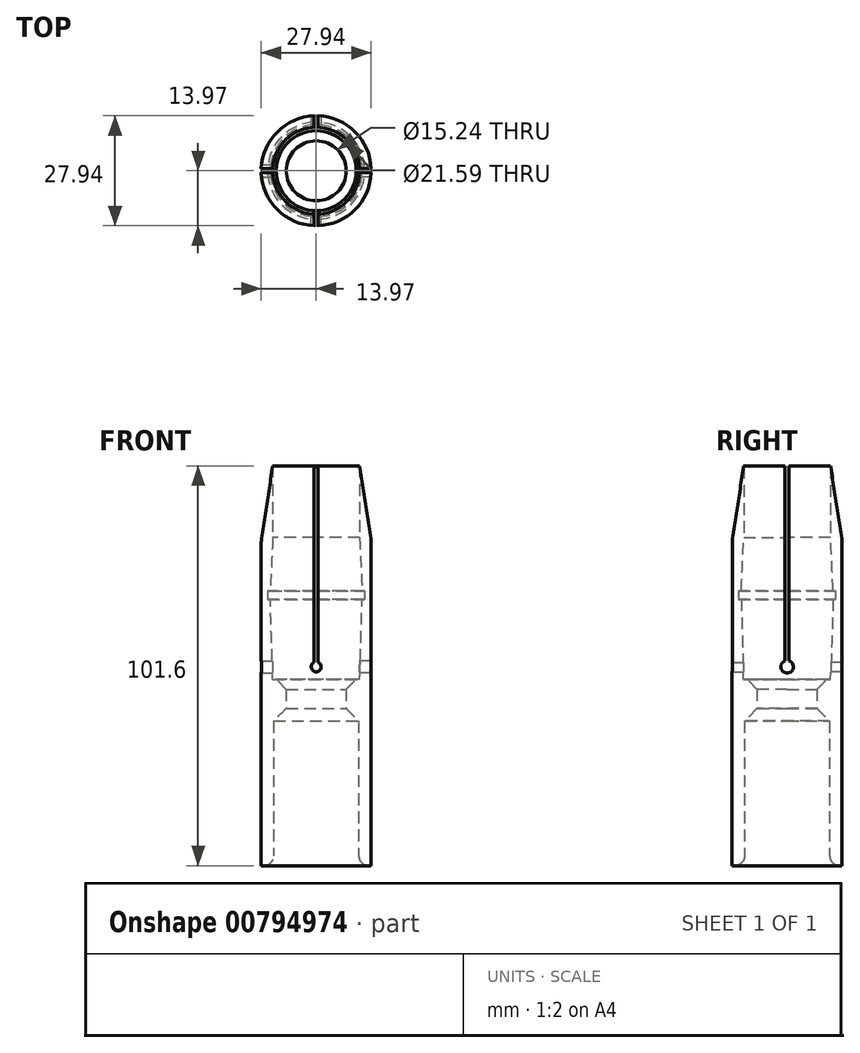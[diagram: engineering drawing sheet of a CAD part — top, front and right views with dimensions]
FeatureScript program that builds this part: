
annotation { "Feature Type Name" : "Feature", "Feature Type Description" : "" }
export const myFeature = defineFeature(function(context is Context, id is Id, definition is map)
    precondition{}
    {
        {
            var Q0;
            Q0=qCreatedBy(makeId("Front.planeOp"),FACE);
            var sketch = newSketch(context, id + "F0", { "sketchPlane" : qUnion([Q0])});
            skLineSegment(sketch, "E0.bottom", {"start": v(10.8, 0) * mm, "end": v(13.97, 0) * mm});
            skLineSegment(sketch, "E0.right", {"start": v(13.97, 0) * mm, "end": v(13.97, 82.55) * mm});
            skLineSegment(sketch, "E1", {"start": v(11.05, 101.6) * mm, "end": v(13.97, 82.55) * mm});
            skLineSegment(sketch, "E2", {"start": v(11.68, 69.85) * mm, "end": v(12.32, 69.85) * mm});
            skLineSegment(sketch, "E3", {"start": v(12.32, 69.85) * mm, "end": v(12.32, 67.7) * mm});
            skLineSegment(sketch, "E4", {"start": v(12.32, 67.7) * mm, "end": v(11.68, 67.7) * mm});
            skLineSegment(sketch, "E5", {"start": v(11.05, 47.37) * mm, "end": v(7.62, 47.37) * mm});
            skLineSegment(sketch, "E6", {"start": v(7.62, 47.37) * mm, "end": v(7.62, 39.95) * mm});
            skLineSegment(sketch, "E7.bottom", {"start": v(7.62, 39.95) * mm, "end": v(10.8, 39.95) * mm});
            skLineSegment(sketch, "E7.right", {"start": v(10.8, 39.95) * mm, "end": v(10.8, 0) * mm});
            skLineSegment(sketch, "E8", {"start": v(11.05, 101.6) * mm, "end": v(11.05, 83.35) * mm});
            skLineSegment(sketch, "E9", {"start": v(11.05, 83.35) * mm, "end": v(11.68, 69.85) * mm});
            skPoint(sketch, "E10", {"position": v(11.68, 67.7) * mm});
            skLineSegment(sketch, "E11", {"start": v(11.05, 47.37) * mm, "end": v(11.68, 67.7) * mm});
            skSolve(sketch);
        }
        {
            var Q0;
            Q0=qCreatedBy(makeId("Front.planeOp"),FACE);
            var sketch = newSketch(context, id + "F1", { "sketchPlane" : qUnion([Q0])});
            skLineSegment(sketch, "E12", {"start": v(0, -19.13) * mm, "end": v(0, 56.04) * mm});
            skSolve(sketch);
        }
        {
            var Q0;
            Q0=makeQuery(id+"F0.imprint","IMPRINT",FACE,{"disambiguationData":[TD([[makeQuery(id+"F0.imprint","IMPRINT",EDGE,{"derivedFrom":sQuery(id+"F0.wireOp",EDGE,"E0.bottom")}),1.0]])]});
            var Q1;
            Q1=sQuery(id+"F1.wireOp",EDGE,"E12");
            revolve(context, id + "F2", {"surfaceOperationType" : NewSurfaceOperationType.NEW, "entities" : qUnion([Q0]), "axis" : qUnion([Q1]), "revolveType" : RevolveType.FULL});
        }
        {
            var Q0;
            Q0=makeQuery(id+"F2.opRevolve","SWEPT_EDGE",EDGE,{"disambiguationData":[OSD([sQuery(id+"F0.wireOp",EDGE,"E0.bottom"),sQuery(id+"F0.wireOp",EDGE,"E7.right")])]});
            fillet(context, id + "F3", {"entities" : qUnion([Q0]), "radius" : 2.54 * mm, "tangentPropagation" : true, "allowEdgeOverflow" : false});
        }
        {
            var Q0;
            Q0=makeQuery(id+"F2.opRevolve","SWEPT_EDGE",EDGE,{"disambiguationData":[OSD([sQuery(id+"F0.wireOp",EDGE,"E5"),sQuery(id+"F0.wireOp",EDGE,"E6")])]});
            chamfer(context, id + "F4", {"entities" : qUnion([Q0]), "width" : 2.54 * mm, "tangentPropagation" : true});
        }
        {
            var Q0;
            Q0=makeQuery(id+"F2.opRevolve","SWEPT_EDGE",EDGE,{"disambiguationData":[OSD([sQuery(id+"F0.wireOp",EDGE,"E7.bottom"),sQuery(id+"F0.wireOp",EDGE,"E7.right")])]});
            chamfer(context, id + "F5", {"entities" : qUnion([Q0]), "width" : 3.17 * mm, "tangentPropagation" : true});
        }
        {
            var Q0;
            Q0=makeQuery(id+"F2.opRevolve","SWEPT_EDGE",EDGE,{"disambiguationData":[OSD([sQuery(id+"F0.wireOp",EDGE,"E0.right"),sQuery(id+"F0.wireOp",EDGE,"E1")])]});
            fillet(context, id + "F6", {"entities" : qUnion([Q0]), "radius" : 7.62 * mm, "tangentPropagation" : true, "allowEdgeOverflow" : false});
        }
        {
            var Q0;
            Q0=qCreatedBy(makeId("Front.planeOp"),FACE);
            var sketch = newSketch(context, id + "F7", { "sketchPlane" : qUnion([Q0])});
            skLineSegment(sketch, "E13.bottom", {"start": v(0.5, 50.55) * mm, "end": v(-0.5, 50.55) * mm});
            skLineSegment(sketch, "E13.top", {"start": v(0.5, 101.35) * mm, "end": v(-0.5, 101.35) * mm});
            skLineSegment(sketch, "E13.left", {"start": v(0.5, 50.55) * mm, "end": v(0.5, 101.35) * mm});
            skLineSegment(sketch, "E13.right", {"start": v(-0.5, 50.55) * mm, "end": v(-0.5, 101.35) * mm});
            skSolve(sketch);
        }
        {
            var Q0;
            Q0=makeQuery(id+"F7.imprint","IMPRINT",FACE,{"disambiguationData":[TD([[makeQuery(id+"F7.imprint","IMPRINT",EDGE,{"derivedFrom":sQuery(id+"F7.wireOp",EDGE,"E13.bottom")}),-1.0]])]});
            extrude(context, id + "F8", {"entities" : qUnion([Q0]), "operationType" : NewBodyOperationType.REMOVE, "endBound" : BoundingType.THROUGH_ALL, "oppositeDirection" : true, "depth" : 25.4 * mm, "offsetDistance" : 25.4 * mm});
        }
        {
            var Q0;
            Q0 = qSketchRegion(id + "F7", true);
            extrude(context, id + "F9", {"entities" : qUnion([Q0]), "operationType" : NewBodyOperationType.REMOVE, "depth" : 25.4 * mm, "offsetDistance" : 25.4 * mm});
        }
        {
            var Q0;
            Q0=qCreatedBy(makeId("Front.planeOp"),FACE);
            var sketch = newSketch(context, id + "F10", { "sketchPlane" : qUnion([Q0])});
            skCircle(sketch, "E14", {"center": v(0, 50.55) * mm, "radius": 1.27 * mm});
            skSolve(sketch);
        }
        {
            var Q0;
            Q0 = qSketchRegion(id + "F10", true);
            extrude(context, id + "F11", {"entities" : qUnion([Q0]), "operationType" : NewBodyOperationType.REMOVE, "endBound" : BoundingType.THROUGH_ALL, "oppositeDirection" : true, "depth" : 25.4 * mm, "offsetDistance" : 25.4 * mm});
        }
        {
            var Q0;
            Q0 = qSketchRegion(id + "F10", true);
            extrude(context, id + "F12", {"entities" : qUnion([Q0]), "operationType" : NewBodyOperationType.REMOVE, "endBound" : BoundingType.THROUGH_ALL, "depth" : 25.4 * mm, "offsetDistance" : 25.4 * mm});
        }
        {
            var Q0;
            Q0=qCreatedBy(makeId("Right.planeOp"),FACE);
            var sketch = newSketch(context, id + "F13", { "sketchPlane" : qUnion([Q0])});
            skLineSegment(sketch, "E15.bottom", {"start": v(0.5, 107.71) * mm, "end": v(-0.5, 107.71) * mm});
            skLineSegment(sketch, "E15.top", {"start": v(0.5, 50.56) * mm, "end": v(-0.5, 50.56) * mm});
            skLineSegment(sketch, "E15.left", {"start": v(0.5, 107.71) * mm, "end": v(0.5, 50.56) * mm});
            skLineSegment(sketch, "E15.right", {"start": v(-0.5, 107.71) * mm, "end": v(-0.5, 50.56) * mm});
            skSolve(sketch);
        }
        {
            var Q0;
            Q0 = qSketchRegion(id + "F13", true);
            extrude(context, id + "F14", {"entities" : qUnion([Q0]), "operationType" : NewBodyOperationType.REMOVE, "endBound" : BoundingType.THROUGH_ALL, "oppositeDirection" : true, "depth" : 25.4 * mm, "offsetDistance" : 25.4 * mm});
        }
        {
            var Q0;
            Q0 = qSketchRegion(id + "F13", true);
            extrude(context, id + "F15", {"entities" : qUnion([Q0]), "operationType" : NewBodyOperationType.REMOVE, "endBound" : BoundingType.THROUGH_ALL, "depth" : 25.4 * mm, "offsetDistance" : 25.4 * mm});
        }
        {
            var Q0;
            Q0=qCreatedBy(makeId("Right.planeOp"),FACE);
            var sketch = newSketch(context, id + "F16", { "sketchPlane" : qUnion([Q0])});
            skCircle(sketch, "E16", {"center": v(0, 50.56) * mm, "radius": 1.59 * mm});
            skSolve(sketch);
        }
        {
            var Q0;
            Q0 = qSketchRegion(id + "F16", true);
            extrude(context, id + "F17", {"entities" : qUnion([Q0]), "operationType" : NewBodyOperationType.REMOVE, "endBound" : BoundingType.THROUGH_ALL, "oppositeDirection" : true, "depth" : 25.4 * mm, "offsetDistance" : 25.4 * mm});
        }
        {
            var Q0;
            Q0 = qSketchRegion(id + "F16", true);
            extrude(context, id + "F18", {"entities" : qUnion([Q0]), "operationType" : NewBodyOperationType.REMOVE, "endBound" : BoundingType.THROUGH_ALL, "depth" : 25.4 * mm, "offsetDistance" : 25.4 * mm});
        }
    });
